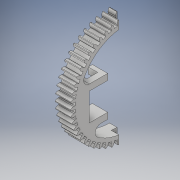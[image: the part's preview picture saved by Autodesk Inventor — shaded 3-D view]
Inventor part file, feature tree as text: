
AUTODESK INVENTOR PART (.ipt)
format: ipt  version: 2018 (Build 220112000, 112)  size: 845,824 bytes
history: native  units: in
note: dims shown in document units (in); Inventor stores cm internally (conversion verified against a paired STEP export)
features: extrude x10, sketch x6, other x2, fillet x1, plane x1
ambient origin geometry x8: Origin, YZ Plane, XZ Plane, XY Plane, X Axis, Y Axis, Z Axis, Center Point
bodies: Body1 (feature_tree)
feature tree (20):
  other  "main sketch"
  extrude  "teeth extrude"  Depth=3.25in
  extrude  "other teeth extrude"  Depth=1.2025in
  extrude  "servo holder extrude"  Depth=0.5in TaperAngle=0.0deg
  fillet  "servo fillet"  Radius=0.5in
  extrude  "Extrusion10"  Depth=0.1875in
  other  "axel work plane"
  extrude  "axel extrude"  Depth=0.0039in
  plane  "Work Plane7"
  extrude  "Extrusion15"  Depth=0.0039in
  sketch  "Sketch10"  dims[d45=0.5in d46=0.0in d48=0.1875in]
  extrude  "Extrusion16"  Depth=0.2in TaperAngle=0.0deg
  extrude  "Extrusion17"  Depth=0.3937in
  extrude  "Extrusion18"  Depth=1.3in TaperAngle=0.0deg
  extrude  "Extrusion19"  Depth=0.3937in
  sketch  "Sketch5"  dims[d0=3.0in d1=3.25in]
  sketch  "Sketch7"  dims[d7=1.2025in d8=1.2025in]
  sketch  "Sketch9"  dims[d13=20.4724in d15=360.0deg d19=0.5in d20=0.0in d23=0.5in d24=0.0in]
  sketch  "Sketch11"  dims[d53=0.15in d56=0.0039in]
  sketch  "Sketch12"  dims[d57=0.0591in d58=0.0039in d59=0.2in d60=0.0in d65=0.24in d66=1.3in d67=0.0in d70=0.311in d71=1.4774in d72=0.0in d73=0.0025in d74=1.4774in d75=0.0in d76=1.4774in d77=0.0in d78=0.1969in d79=0.25in d80=39.3701in d81=0.1969in d82=0.0in d83=0.0in d84=0.3937in d85=0.0in]
